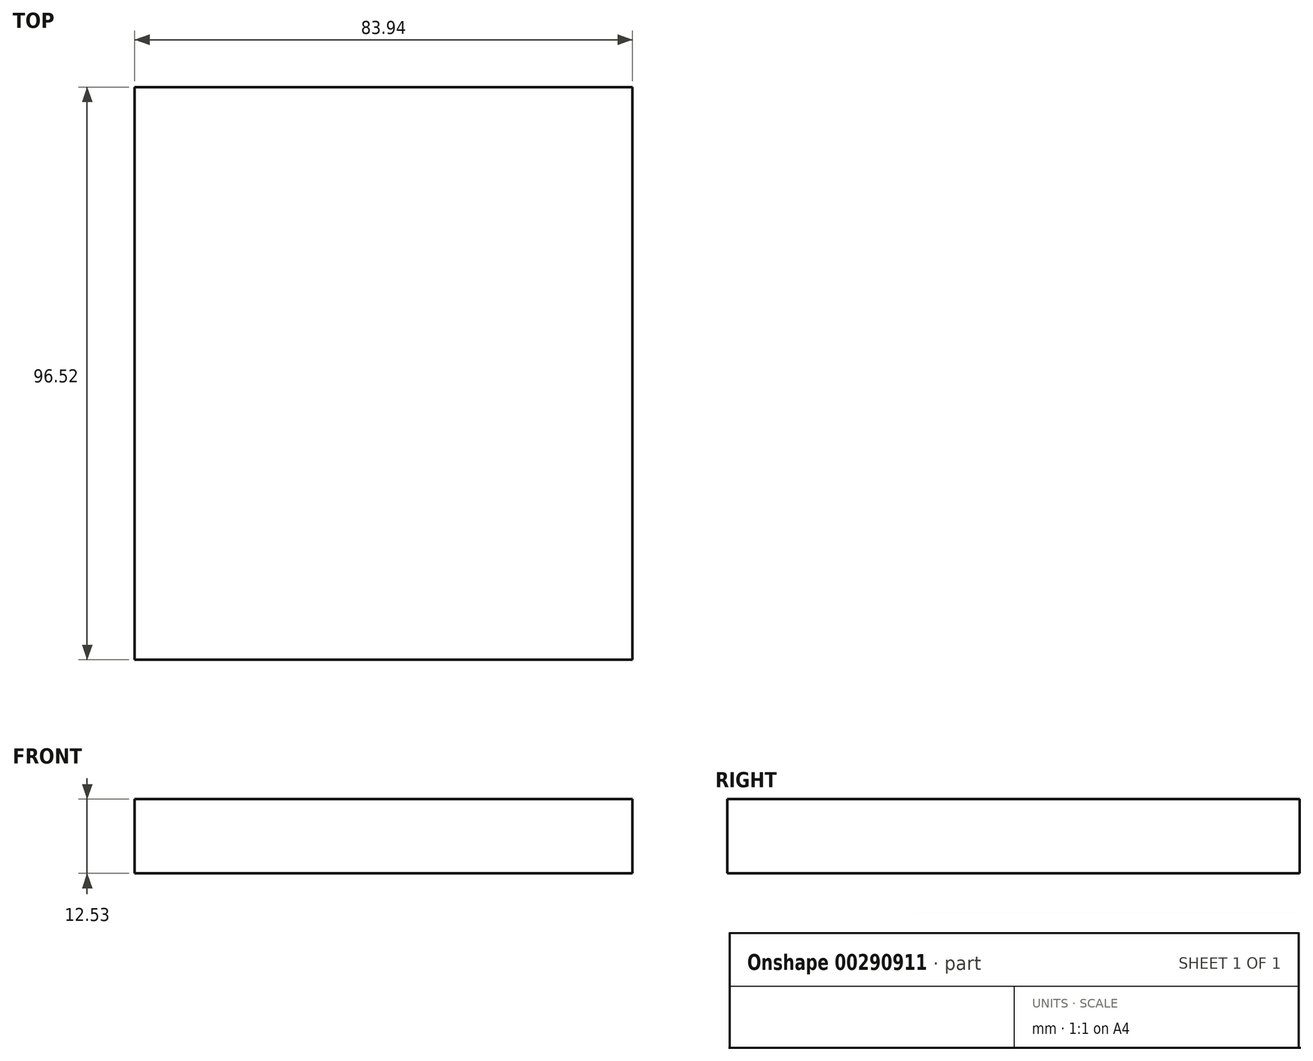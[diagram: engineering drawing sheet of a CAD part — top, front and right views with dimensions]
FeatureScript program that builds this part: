
annotation { "Feature Type Name" : "Feature", "Feature Type Description" : "" }
export const myFeature = defineFeature(function(context is Context, id is Id, definition is map)
    precondition{}
    {
        {
            var Q0;
            Q0=qCreatedBy(makeId("Front.planeOp"),FACE);
            var sketch = newSketch(context, id + "F0", { "sketchPlane" : qUnion([Q0])});
            skLineSegment(sketch, "E0.bottom", {"start": v(-43.72, 17.05) * mm, "end": v(40.22, 17.05) * mm});
            skLineSegment(sketch, "E0.top", {"start": v(-43.72, 4.52) * mm, "end": v(40.22, 4.52) * mm});
            skLineSegment(sketch, "E0.left", {"start": v(-43.72, 17.05) * mm, "end": v(-43.72, 4.52) * mm});
            skLineSegment(sketch, "E0.right", {"start": v(40.22, 17.05) * mm, "end": v(40.22, 4.52) * mm});
            skSolve(sketch);
        }
        {
            var Q0;
            Q0 = qSketchRegion(id + "F0", true);
            extrude(context, id + "F1", {"entities" : qUnion([Q0]), "depth" : 96.52 * mm});
        }
    });
